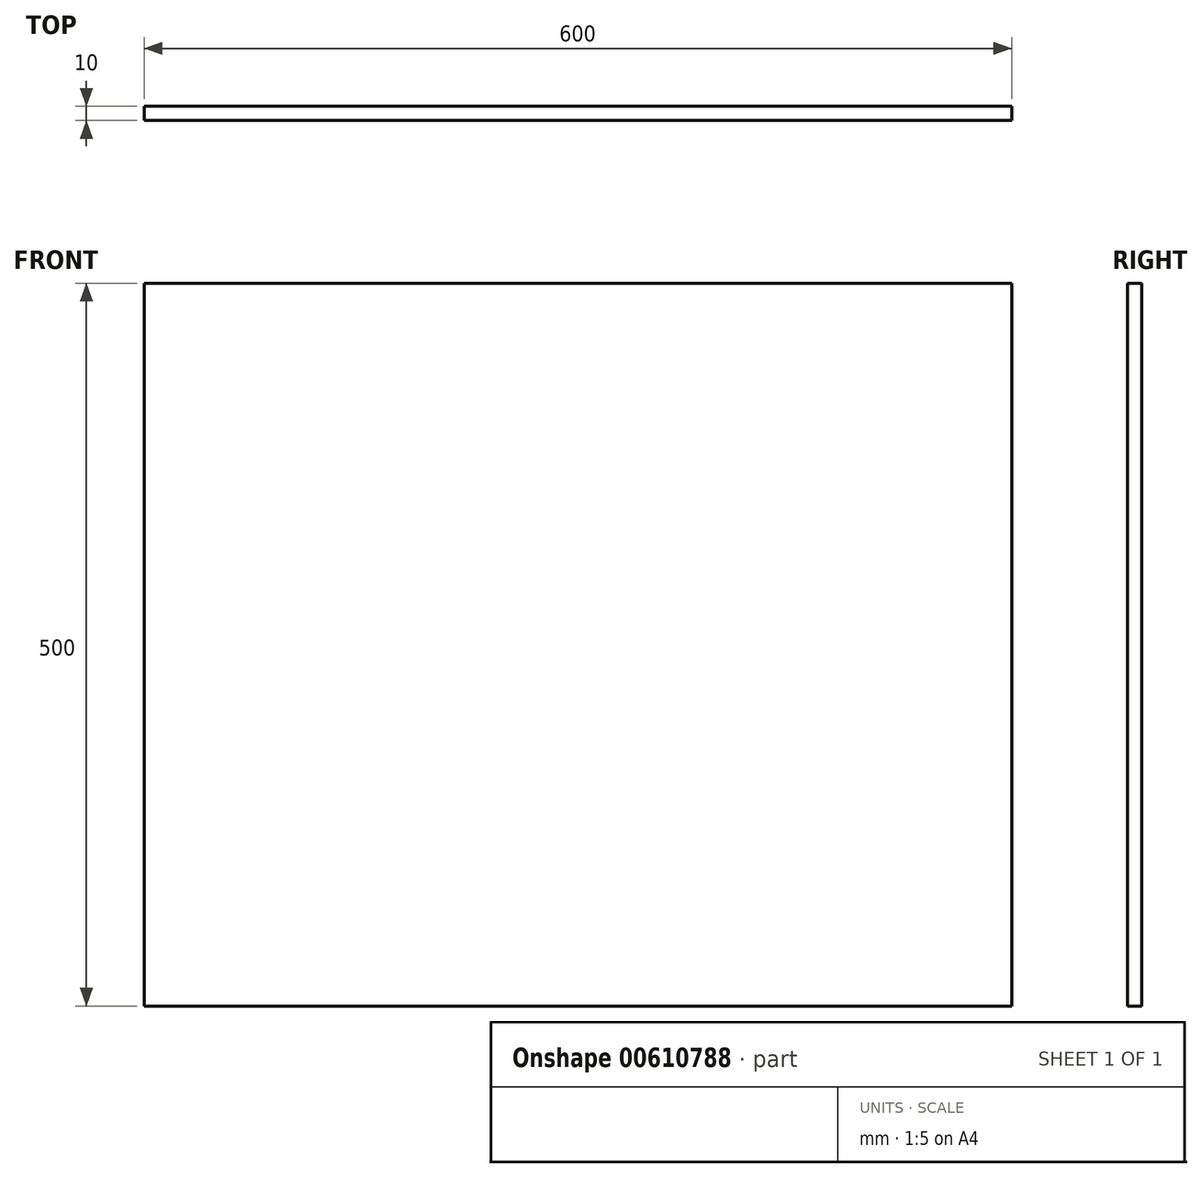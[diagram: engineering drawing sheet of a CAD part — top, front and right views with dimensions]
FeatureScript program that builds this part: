
annotation { "Feature Type Name" : "Feature", "Feature Type Description" : "" }
export const myFeature = defineFeature(function(context is Context, id is Id, definition is map)
    precondition{}
    {
        {
            var Q0;
            Q0=qCreatedBy(makeId("Front.planeOp"),FACE);
            var sketch = newSketch(context, id + "F0", { "sketchPlane" : qUnion([Q0])});
            skLineSegment(sketch, "E0.bottom", {"start": v(-275.57, 244.67) * mm, "end": v(324.43, 244.67) * mm});
            skLineSegment(sketch, "E0.top", {"start": v(-275.57, -255.33) * mm, "end": v(324.43, -255.33) * mm});
            skLineSegment(sketch, "E0.left", {"start": v(-275.57, 244.67) * mm, "end": v(-275.57, -255.33) * mm});
            skLineSegment(sketch, "E0.right", {"start": v(324.43, 244.67) * mm, "end": v(324.43, -255.33) * mm});
            skSolve(sketch);
        }
        {
            var Q0;
            Q0 = qSketchRegion(id + "F0", true);
            extrude(context, id + "F1", {"entities" : qUnion([Q0]), "depth" : 10 * mm, "offsetDistance" : 25 * mm});
        }
    });
